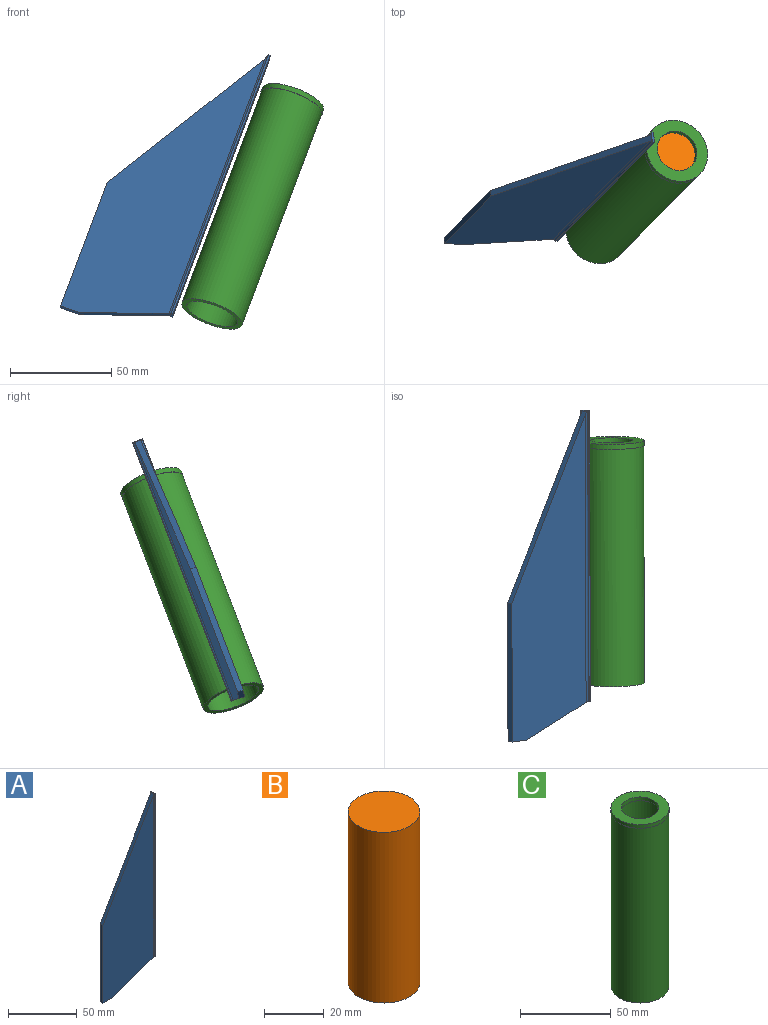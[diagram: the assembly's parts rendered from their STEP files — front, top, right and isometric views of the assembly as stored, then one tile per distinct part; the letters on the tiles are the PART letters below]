
ASSEMBLY  parts=3 mates=4
PART A: 22 faces, bbox 53.7x6x160.2 mm
  f0: cylinder r=19.05mm len=144.53mm, axis (0,0,1), area 30.7mm2, adj f12,f14,f15,f18
  f1: cylinder r=19.05mm len=4.75mm, axis (0,0,1), area 1.3mm2, adj f10,f13,f18
  f2: cylinder r=19.05mm len=144.53mm, axis (0,0,1), area 30.7mm2, adj f11,f12,f17,f18
  f3: plane 5.17x0.95mm, normal (0,0,-1), area 4.9mm2, adj f12,f15,f16,f17
  f4: plane 90.86x52.55mm, normal (-0.87,0,0.5), area 314.5mm2, adj f5,f8,f9,f10,f11,f13,f14
  f5: plane 68.75x3mm, normal (-1,0,0), area 206.3mm2, adj f4,f6,f8,f9
  f6: plane 10x3mm, normal (0,0,-1), area 30mm2, adj f5,f7,f8,f9
  f7: plane 42.19x15.37mm, normal (0.34,0,-0.94), area 134.8mm2, adj f6,f8,f9,f11,f12,f14
  f8: plane 157.94x51.5mm, normal (0,-1,0), area 5523.5mm2, adj f4,f5,f6,f7,f14
  f9: plane 157.94x51.5mm, normal (0,1,0), area 5523.5mm2, adj f4,f5,f6,f7,f11
  f10: bspline ~2.9x0.61mm, area 0.5mm2, adj f1,f4,f11
  f11: cylinder r=1mm len=144.84mm, axis (0,0,1), area 207.7mm2, adj f2,f4,f7,f9,f10,f12
  f12: cylinder r=1mm len=5.17mm, axis (0,-1,0), area 1.5mm2, adj f0,f2,f3,f7,f11,f14
  f13: bspline ~2.9x0.61mm, area 0.5mm2, adj f1,f4,f14
  f14: cylinder r=1mm len=144.84mm, axis (0,0,1), area 207.7mm2, adj f0,f4,f7,f8,f12,f13
  f15: plane 144.53x0.95mm, normal (0,-1,0), area 137.3mm2, adj f0,f3,f16,f18
  f16: plane 144.53x5.17mm, normal (1,0,0), area 732.3mm2, adj f3,f15,f17,f18,f19,f20,f21
  f17: plane 144.53x0.95mm, normal (0,1,0), area 137.3mm2, adj f2,f3,f16,f18
  f18: plane 5.17x1.13mm, normal (0,0,1), area 5.5mm2, adj f0,f1,f2,f15,f16,f17
  f19: cone r=1.27mm half-angle=10deg, axis (1,0,0), area 29.2mm2, adj f16
  f20: cone r=1.27mm half-angle=10deg, axis (1,0,0), area 29.2mm2, adj f16
  f21: cone r=1.27mm half-angle=10deg, axis (1,0,0), area 29.2mm2, adj f16
PART B: 6 faces, bbox 24x24x70 mm
  f0: cylinder r=12mm len=70mm, axis (0,0,1), area 5277.9mm2, adj f1,f5
  f1: plane 24x24mm, normal (0,0,-1), area 168.9mm2, adj f0,f2
  f2: sphere r=16.24mm, area 306mm2, adj f1,f3
  f3: cylinder r=1.5mm len=6.27mm, axis (0,0,1), area 59.1mm2, adj f2,f4
  f4: sphere r=1.9mm, area 8.7mm2, adj f3
  f5: plane 24x24mm, normal (0,0,1), area 452.4mm2, adj f0
PART C: 8 faces, bbox 32.1x32.1x120.5 mm
  f0: plane 32.1x32.1mm, normal (0,0,-1), area 21.5mm2, adj f1,f6
  f1: cylinder r=15.83mm len=118mm, axis (0,0,1), area 11740.3mm2, adj f0,f7
  f2: cylinder r=13.33mm len=118mm, axis (0,0,1), area 9886.8mm2, adj f3,f7
  f3: plane 26.67x26.67mm, normal (0,0,-1), area 223.1mm2, adj f2,f4
  f4: cylinder r=10.34mm len=20.67mm, axis (0,0,1), area 162.3mm2, adj f3,f5
  f5: plane 32.1x32.1mm, normal (0,0,1), area 473.7mm2, adj f4,f6
  f6: cylinder r=16.05mm len=32.1mm, axis (0,0,1), area 252.1mm2, adj f0,f5
  f7: plane 31.67x31.67mm, normal (0,0,-1), area 229.1mm2, adj f1,f2
PLACE A rot(axis=(-0.71,0.7,0),28.2deg) t=(188.04,185.15,135.74)mm
PLACE B rot(axis=(-0.71,0.7,0),28.2deg) t=(111.66,107.6,-67.16)mm
PLACE C rot(axis=(-0.71,0.7,0),28.2deg) t=(188.37,185.49,136.62)mm
MATE planar C.f1 <-> A.f0  axis (-0.33,-0.34,-0.88) through (94.91,90.59,-111.66)mm
MATE slider B.f0 <-> C.f1  axis (0.33,0.34,0.88) through (134.88,131.18,-5.47)mm
MATE planar B.f0 <-> C.f1  axis (0.33,0.34,0.88) through (134.88,131.18,-5.47)mm
MATE slider C.f1 <-> A.f0  axis (-0.33,-0.34,-0.88) through (94.91,90.59,-111.66)mm
